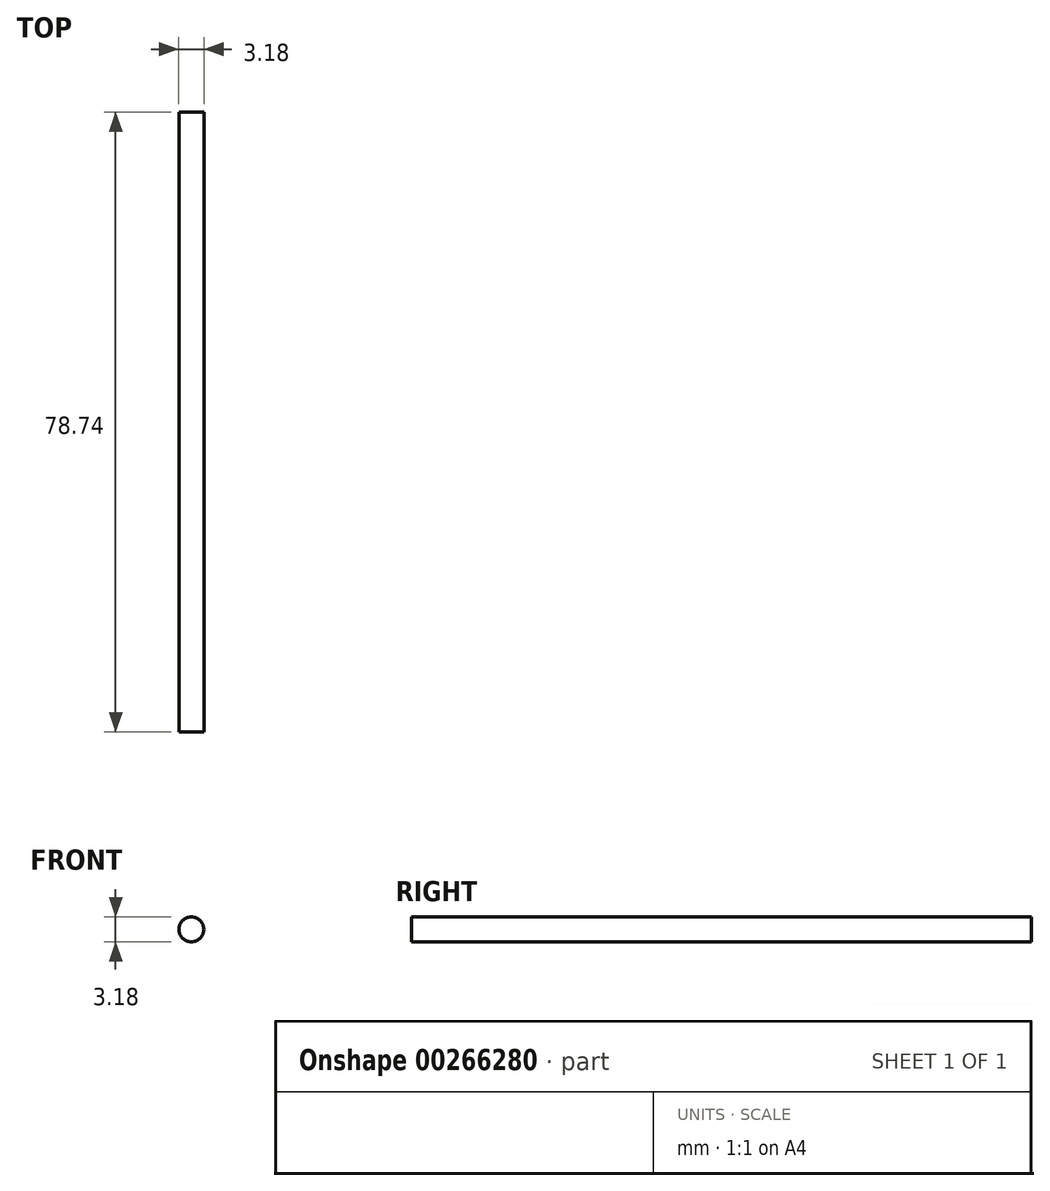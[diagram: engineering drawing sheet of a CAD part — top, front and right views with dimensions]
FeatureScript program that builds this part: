
annotation { "Feature Type Name" : "Feature", "Feature Type Description" : "" }
export const myFeature = defineFeature(function(context is Context, id is Id, definition is map)
    precondition{}
    {
        {
            var Q0;
            Q0=qCreatedBy(makeId("Front.planeOp"),FACE);
            var sketch = newSketch(context, id + "F0", { "sketchPlane" : qUnion([Q0])});
            skCircle(sketch, "E0", {"center": v(0, 0) * mm, "radius": 1.59 * mm});
            skSolve(sketch);
        }
        {
            var Q0;
            Q0=qSketchRegion(id+"F0",true);
            extrude(context, id + "F1", {"entities" : qUnion([Q0]), "endBound" : BoundingType.SYMMETRIC, "depth" : 78.74 * mm});
        }
    });
